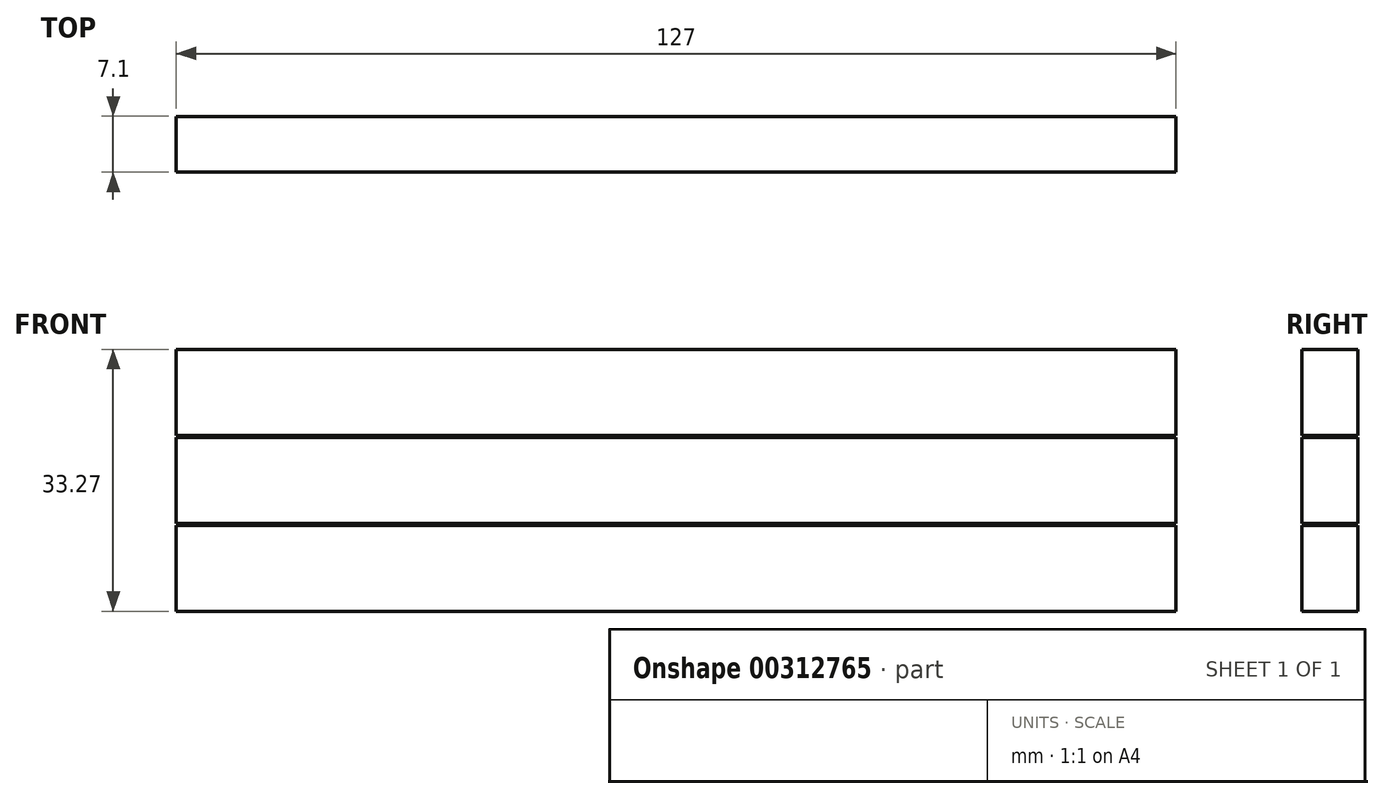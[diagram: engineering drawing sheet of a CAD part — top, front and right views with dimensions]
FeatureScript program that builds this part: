
annotation { "Feature Type Name" : "Feature", "Feature Type Description" : "" }
export const myFeature = defineFeature(function(context is Context, id is Id, definition is map)
    precondition{}
    {
        {
            var Q0;
            Q0=qCreatedBy(makeId("Top.planeOp"),FACE);
            var sketch = newSketch(context, id + "F0", { "sketchPlane" : qUnion([Q0])});
            skLineSegment(sketch, "E0.bottom", {"start": v(-61.57, -30.07) * mm, "end": v(65.43, -30.07) * mm});
            skLineSegment(sketch, "E0.top", {"start": v(-61.57, -37.17) * mm, "end": v(65.43, -37.17) * mm});
            skLineSegment(sketch, "E0.left", {"start": v(-61.57, -37.17) * mm, "end": v(-61.57, -30.07) * mm});
            skLineSegment(sketch, "E0.right", {"start": v(65.43, -37.17) * mm, "end": v(65.43, -30.07) * mm});
            skSolve(sketch);
        }
        {
            var Q0;
            Q0=makeQuery(id+"F0.imprint","IMPRINT",FACE,{"disambiguationData":[TD([[makeQuery(id+"F0.imprint","IMPRINT",EDGE,{"derivedFrom":sQuery(id+"F0.wireOp",EDGE,"E0.bottom")}),-1.0]])]});
            extrude(context, id + "F1", {"entities" : qUnion([Q0]), "depth" : 10.92 * mm});
        }
        {
            var Q0;
            Q0=makeQuery(id+"F1.opExtrude","SWEPT_BODY",BODY,{"disambiguationData":[OSD([sQuery(id+"F0.wireOp",EDGE,"E0.bottom"),sQuery(id+"F0.wireOp",EDGE,"E0.top"),sQuery(id+"F0.wireOp",EDGE,"E0.left"),sQuery(id+"F0.wireOp",EDGE,"E0.right")])]});
            transform(context, id + "F2", {"entities" : qUnion([Q0]), "transformType" : TransformType.TRANSLATION_3D, "dx" : 0 * mm, "dy" : 25.4 * mm, "dz" : 11.18 * mm, "makeCopy" : true});
        }
        {
            var Q0;
            Q0=makeQuery(id+"F2.opPattern","COPY",BODY,{"derivedFrom":makeQuery(id+"F1.opExtrude","SWEPT_BODY",BODY,{"disambiguationData":[OSD([sQuery(id+"F0.wireOp",EDGE,"E0.bottom"),sQuery(id+"F0.wireOp",EDGE,"E0.top"),sQuery(id+"F0.wireOp",EDGE,"E0.left"),sQuery(id+"F0.wireOp",EDGE,"E0.right")])]}),"instanceName":"1"});
            deleteBodies(context, id + "F3", {"entities" : qUnion([Q0])});
        }
        {
            var Q0;
            Q0=makeQuery(id+"F1.opExtrude","SWEPT_BODY",BODY,{"disambiguationData":[OSD([sQuery(id+"F0.wireOp",EDGE,"E0.bottom"),sQuery(id+"F0.wireOp",EDGE,"E0.top"),sQuery(id+"F0.wireOp",EDGE,"E0.left"),sQuery(id+"F0.wireOp",EDGE,"E0.right")])]});
            transform(context, id + "F4", {"entities" : qUnion([Q0]), "transformType" : TransformType.TRANSLATION_3D, "dx" : 0 * mm, "dy" : 0 * mm, "dz" : 11.18 * mm, "makeCopy" : true});
        }
        {
            var Q0;
            Q0=makeQuery(id+"F4.opPattern","COPY",BODY,{"derivedFrom":makeQuery(id+"F1.opExtrude","SWEPT_BODY",BODY,{"disambiguationData":[OSD([sQuery(id+"F0.wireOp",EDGE,"E0.bottom"),sQuery(id+"F0.wireOp",EDGE,"E0.top"),sQuery(id+"F0.wireOp",EDGE,"E0.left"),sQuery(id+"F0.wireOp",EDGE,"E0.right")])]}),"instanceName":"1"});
            transform(context, id + "F5", {"entities" : qUnion([Q0]), "transformType" : TransformType.TRANSLATION_3D, "dx" : 0 * mm, "dy" : 0 * mm, "dz" : 11.18 * mm, "makeCopy" : true});
        }
    });
